# Revit family: ZETA_Коробка_Клемная_КЗНС-48
name_source: partatom
category: Электрические приборы
units: mm (PartAtom-declared; Revit-internal decimal feet)

## family parameters
Всегда вертикально = Да
На основе рабочей плоскости = Нет
Общий = Нет
При загрузке вырезать с полостями = Нет
Размер круглого соединителя = Использовать диаметр
Сохранять ориентацию аннотаций = Нет
Тип детали = Нормальный
Точка принадлежности помещению = Да

## types (2) — shared parameters
ADSK_URL документации изделия = https://nzeta.ru
ADSK_URL страницы изделия = https://nzeta.ru
ADSK_Версия Revit = 2021
ADSK_Версия семейства = v.1
ADSK_Единица измерения = шт
ADSK_Завод-изготовитель = АО «ЗЭТА»
ADSK_Классификация нагрузок = Прочее
ADSK_Количество = 1
ADSK_Количество фаз = 1
ADSK_Количество фаз числовое = 1
ADSK_Коэффициент мощности = 1
ADSK_Материал наименование = Сталь оцинкованная
ADSK_Наименование краткое = КЗНС-48
ADSK_Напряжение = 230 В
ADSK_Номинальная мощность = 0 Вт
ADSK_Обозначение = KK
ADSK_Полная мощность = 0 В·А
ADSK_Размер_Высота = 106 мм
ADSK_Размер_Длина = 345 мм
ADSK_Размер_Ширина = 266 мм
ADSK_Ток = 0 А
D1 = 25 мм
D2 = 32 мм
D3 = 40 мм
URL = https://nzeta.ru
Изготавливается по = ТУ 27.33.13.120-047-99856433-2020
Изготовитель = АО «ЗЭТА»
Изображение = <Нет>
Использовать масштаб аннотаций = Нет
Количество зажимов = 10
Корпус_Высота = 71 мм
Корпус_Длина = 315 мм
Корпус_Ширина = 237 мм
Крепления_Длина = 384 мм
Крепления_Ширина = 88 мм
Крышка_Высота = 16 мм
Крышка_Длина = 924 мм
Крышка_Ширина = 610 мм
КрышкаВерх_Длина = 209 мм
КрышкаВерх_Ширина = 137 мм
КрышкаОснование_Длина = 273 мм
КрышкаОснование_Ширина = 198 мм
Марка = 1
Материал корпуса = Zeta_Сталь оцинкованная
МеталическаяЗаглушка_Привязка = 100 мм
Номинальный ток = до 25А
Описание = Коробки клеммные с наборными зажимами КЗНС с латунными кабельными
вводами применяются для соединения и разветвления вторичных и силовых
электрических цепей, выполняемых контрольными кабелями с числом жил до 52 и
силовыми кабелями с алюминиевыми или медными жилами сечением 1,5—4 мм2.
Отверстие1_Привязка = 35 мм
Отверстие2_Привязка = 35 мм
Сертификат = RU C-RU.АД84.В.00192/20
Сечение жил = до 4 мм2
Температура эксплуатации = от -40 до +60 °С
УГО_Высота = 5 мм
УГО_Длина = 10 мм
zero-valued in all types: Отметка по умолчанию

## per-type parameters (varying)
| type | ADSK_Код изделия | ADSK_Марка | ADSK_Масса | ADSK_Масса_Текст | ADSK_Наименование | ADSK_Степень защиты_IP | Климатическое исполнение |
| 48_IP54 | zeta30358 | КК КЗНС-48 У2 IP54 | 4.9 | 4.9 | Коробка с зажимами наборными КЗНС-48 У2 IP54 пластиковый ввод ГОФРОМАТИК | IP54 | У2 |
| 48_IP65 | zeta30350 | КК КЗНС-32 УХЛ1,5 IP65 | 5.42 | 5.42 | Коробка с зажимами наборными КЗНС-48 УХЛ1,5  IP65  латунный ввод ГОФРОМАТИК | IP65 | УХЛ1,5 |

## geometry (parser evidence)
native form markers: Sweep x3
no freeform markers — native parametric forms only
